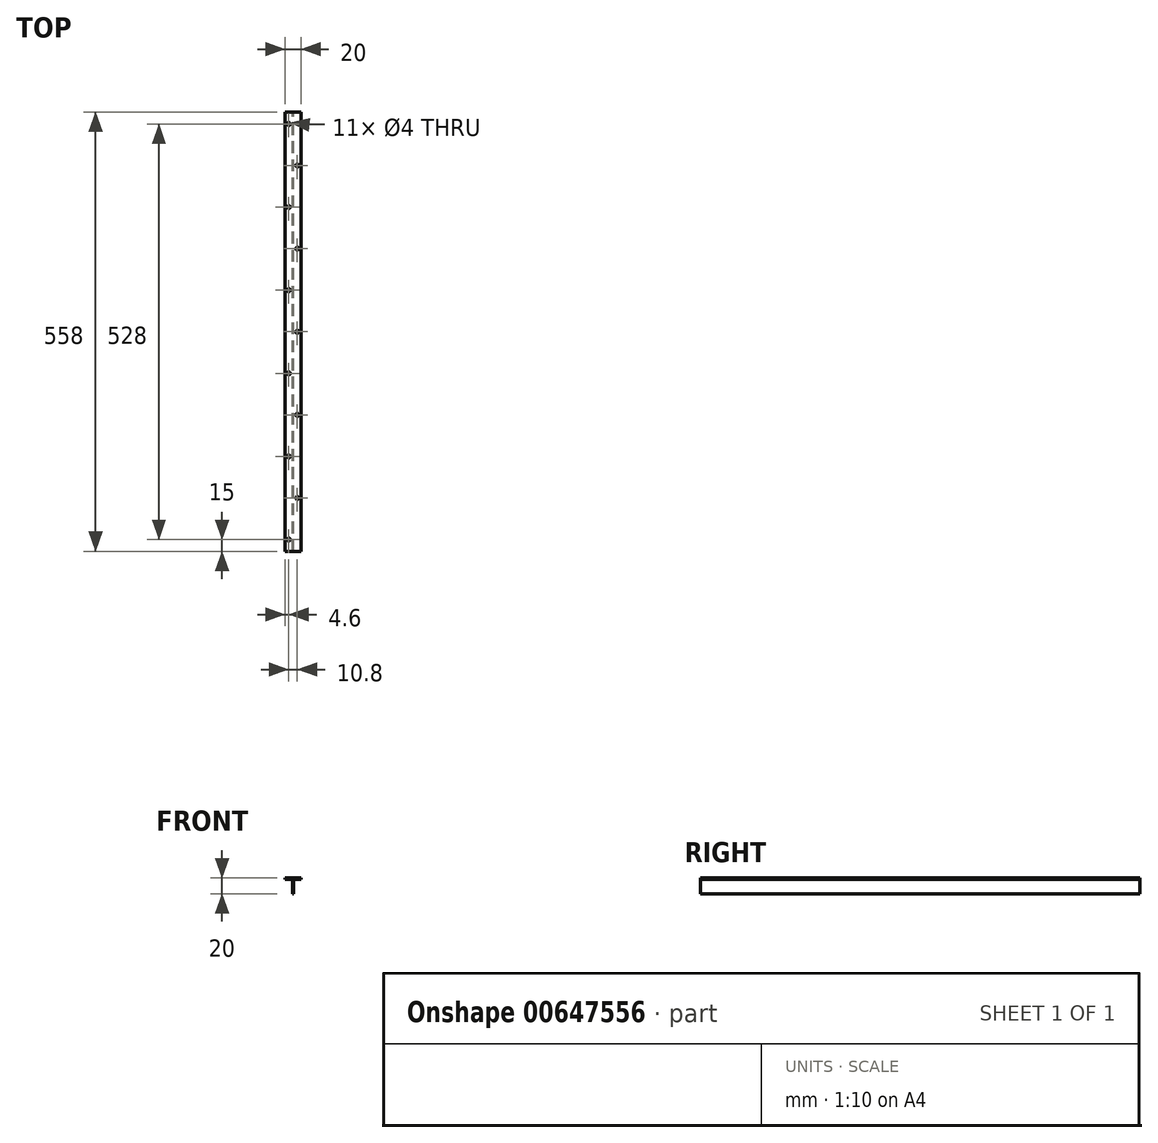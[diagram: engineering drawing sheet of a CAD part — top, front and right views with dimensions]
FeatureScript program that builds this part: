
annotation { "Feature Type Name" : "Feature", "Feature Type Description" : "" }
export const myFeature = defineFeature(function(context is Context, id is Id, definition is map)
    precondition{}
    {
        {
            var Q0;
            Q0=qCreatedBy(makeId("Front.planeOp"),FACE);
            var sketch = newSketch(context, id + "F0", { "sketchPlane" : qUnion([Q0])});
            skLineSegment(sketch, "E0", {"start": v(-10, 0) * mm, "end": v(10, 0) * mm});
            skLineSegment(sketch, "E1", {"start": v(10, 0) * mm, "end": v(10, -1.6) * mm});
            skLineSegment(sketch, "E2", {"start": v(10, -1.6) * mm, "end": v(0.8, -1.6) * mm});
            skLineSegment(sketch, "E3", {"start": v(0.8, -1.6) * mm, "end": v(0.8, -20) * mm});
            skLineSegment(sketch, "E4", {"start": v(0.8, -20) * mm, "end": v(-0.8, -20) * mm});
            skLineSegment(sketch, "E5", {"start": v(-0.8, -20) * mm, "end": v(-0.8, -1.6) * mm});
            skLineSegment(sketch, "E6", {"start": v(-0.8, -1.6) * mm, "end": v(-10, -1.6) * mm});
            skLineSegment(sketch, "E7", {"start": v(-10, -1.6) * mm, "end": v(-10, 0) * mm});
            skPoint(sketch, "E8", {"position": v(0, 0) * mm});
            skPoint(sketch, "E9", {"position": v(0, -20) * mm});
            skSolve(sketch);
        }
        {
            var Q0;
            Q0=makeQuery(id+"F0.imprint","IMPRINT",FACE,{"disambiguationData":[TD([[makeQuery(id+"F0.imprint","IMPRINT",EDGE,{"derivedFrom":sQuery(id+"F0.wireOp",EDGE,"E0")}),-1.0]])]});
            extrude(context, id + "F1", {"entities" : qUnion([Q0]), "depth" : 558 * mm, "offsetDistance" : 25 * mm});
        }
        {
            var Q0;
            Q0=makeQuery(id+"F1.opExtrude","SWEPT_FACE",FACE,{"disambiguationData":[OSD([sQuery(id+"F0.wireOp",EDGE,"E0")])]});
            var sketch = newSketch(context, id + "F2", { "sketchPlane" : qUnion([Q0])});
            skLineSegment(sketch, "E10.0", {"start": v(0.8, -558) * mm, "end": v(0.8, 0) * mm, "construction": true});
            skLineSegment(sketch, "E11.0", {"start": v(10, -558) * mm, "end": v(10, 0) * mm, "construction": true});
            skLineSegment(sketch, "E12.0", {"start": v(10, -558) * mm, "end": v(0.8, -558) * mm, "construction": true});
            skLineSegment(sketch, "E13.0", {"start": v(-0.8, -558) * mm, "end": v(-10, -558) * mm, "construction": true});
            skLineSegment(sketch, "E14.0", {"start": v(-10, -558) * mm, "end": v(-10, 0) * mm, "construction": true});
            skLineSegment(sketch, "E15.0", {"start": v(-0.8, -558) * mm, "end": v(-0.8, 0) * mm, "construction": true});
            skLineSegment(sketch, "E16.0", {"start": v(-10, 0) * mm, "end": v(10, 0) * mm, "construction": true});
            skLineSegment(sketch, "E17", {"start": v(-11.64, -543) * mm, "end": v(11.46, -543) * mm, "construction": true});
            skLineSegment(sketch, "E18", {"start": v(-14.69, -15) * mm, "end": v(15.75, -15) * mm, "construction": true});
            skLineSegment(sketch, "E19.0.1.0", {"start": v(-11.64, -490.2) * mm, "end": v(11.46, -490.2) * mm, "construction": true});
            skLineSegment(sketch, "E19.0.2.0", {"start": v(-11.64, -437.4) * mm, "end": v(11.46, -437.4) * mm, "construction": true});
            skLineSegment(sketch, "E19.0.3.0", {"start": v(-11.64, -384.6) * mm, "end": v(11.46, -384.6) * mm, "construction": true});
            skLineSegment(sketch, "E19.0.4.0", {"start": v(-11.64, -331.8) * mm, "end": v(11.46, -331.8) * mm, "construction": true});
            skLineSegment(sketch, "E19.0.5.0", {"start": v(-11.64, -279) * mm, "end": v(11.46, -279) * mm, "construction": true});
            skLineSegment(sketch, "E19.0.6.0", {"start": v(-11.64, -226.2) * mm, "end": v(11.46, -226.2) * mm, "construction": true});
            skLineSegment(sketch, "E19.0.7.0", {"start": v(-11.64, -173.4) * mm, "end": v(11.46, -173.4) * mm, "construction": true});
            skLineSegment(sketch, "E19.0.8.0", {"start": v(-11.64, -120.6) * mm, "end": v(11.46, -120.6) * mm, "construction": true});
            skLineSegment(sketch, "E19.direction1", {"start": v(-11.64, -543) * mm, "end": v(13.36, -543) * mm, "construction": true});
            skLineSegment(sketch, "E19.direction2", {"start": v(-11.64, -543) * mm, "end": v(-11.64, -490.2) * mm, "construction": true});
            skLineSegment(sketch, "E20.0.0.9", {"start": v(-11.64, -67.8) * mm, "end": v(11.46, -67.8) * mm, "construction": true});
            skLineSegment(sketch, "E21.0.0.10", {"start": v(-11.64, -15) * mm, "end": v(11.46, -15) * mm, "construction": true});
            skLineSegment(sketch, "E22", {"start": v(-10, -553.48) * mm, "end": v(-0.8, -553.48) * mm, "construction": true});
            skLineSegment(sketch, "E23", {"start": v(-5.4, -543) * mm, "end": v(-5.4, -15) * mm, "construction": true});
            skPoint(sketch, "E23.startSnap0", {"position": v(-5.4, -553.48) * mm});
            skLineSegment(sketch, "E24", {"start": v(0.8, -553.15) * mm, "end": v(10, -553.15) * mm, "construction": true});
            skLineSegment(sketch, "E25", {"start": v(5.4, -543) * mm, "end": v(5.4, 0) * mm, "construction": true});
            skPoint(sketch, "E25.startSnap0", {"position": v(5.4, -553.15) * mm});
            skPoint(sketch, "E26", {"position": v(5.4, -490.2) * mm});
            skPoint(sketch, "E27", {"position": v(-5.4, -437.4) * mm});
            skPoint(sketch, "E28", {"position": v(5.4, -384.6) * mm});
            skPoint(sketch, "E29", {"position": v(-5.4, -331.8) * mm});
            skPoint(sketch, "E30", {"position": v(5.4, -279) * mm});
            skPoint(sketch, "E31", {"position": v(-5.4, -226.2) * mm});
            skPoint(sketch, "E32", {"position": v(5.4, -173.4) * mm});
            skPoint(sketch, "E33", {"position": v(-5.4, -120.6) * mm});
            skPoint(sketch, "E34", {"position": v(5.4, -67.8) * mm});
            skPoint(sketch, "E35", {"position": v(-5.4, -15) * mm});
            skSolve(sketch);
        }
        {
            var Q0;
            Q0=sQuery(id+"F2.wireOp",VERTEX,"E23.start");
            var Q1;
            Q1=sQuery(id+"F2.wireOp",VERTEX,"E26");
            var Q2;
            Q2=sQuery(id+"F2.wireOp",VERTEX,"E27");
            var Q3;
            Q3=sQuery(id+"F2.wireOp",VERTEX,"E28");
            var Q4;
            Q4=sQuery(id+"F2.wireOp",VERTEX,"E29");
            var Q5;
            Q5=sQuery(id+"F2.wireOp",VERTEX,"E30");
            var Q6;
            Q6=sQuery(id+"F2.wireOp",VERTEX,"E31");
            var Q7;
            Q7=sQuery(id+"F2.wireOp",VERTEX,"E32");
            var Q8;
            Q8=sQuery(id+"F2.wireOp",VERTEX,"E33");
            var Q9;
            Q9=sQuery(id+"F2.wireOp",VERTEX,"E34");
            var Q10;
            Q10=sQuery(id+"F2.wireOp",VERTEX,"E35");
            var Q11;
            Q11=makeQuery(id+"F1.opExtrude","SWEPT_BODY",BODY,{"disambiguationData":[OSD([sQuery(id+"F0.wireOp",EDGE,"E0"),sQuery(id+"F0.wireOp",EDGE,"E1"),sQuery(id+"F0.wireOp",EDGE,"E2"),sQuery(id+"F0.wireOp",EDGE,"E3"),sQuery(id+"F0.wireOp",EDGE,"E4"),sQuery(id+"F0.wireOp",EDGE,"E5"),sQuery(id+"F0.wireOp",EDGE,"E6"),sQuery(id+"F0.wireOp",EDGE,"E7")])]});
            hole(context, id + "F3", {"style" : HoleStyle.SIMPLE, "endStyle" : HoleEndStyle.THROUGH, "holeDiameter" : 4 * mm, "majorDiameter" : 5 * mm, "isTappedThrough" : true, "tappedDepth" : 12 * mm, "tapClearance" : 3, "startFromSketch" : true, "locations" : qUnion([Q0, Q1, Q2, Q3, Q4, Q5, Q6, Q7, Q8, Q9, Q10]), "scope" : qUnion([Q11])});
        }
    });
